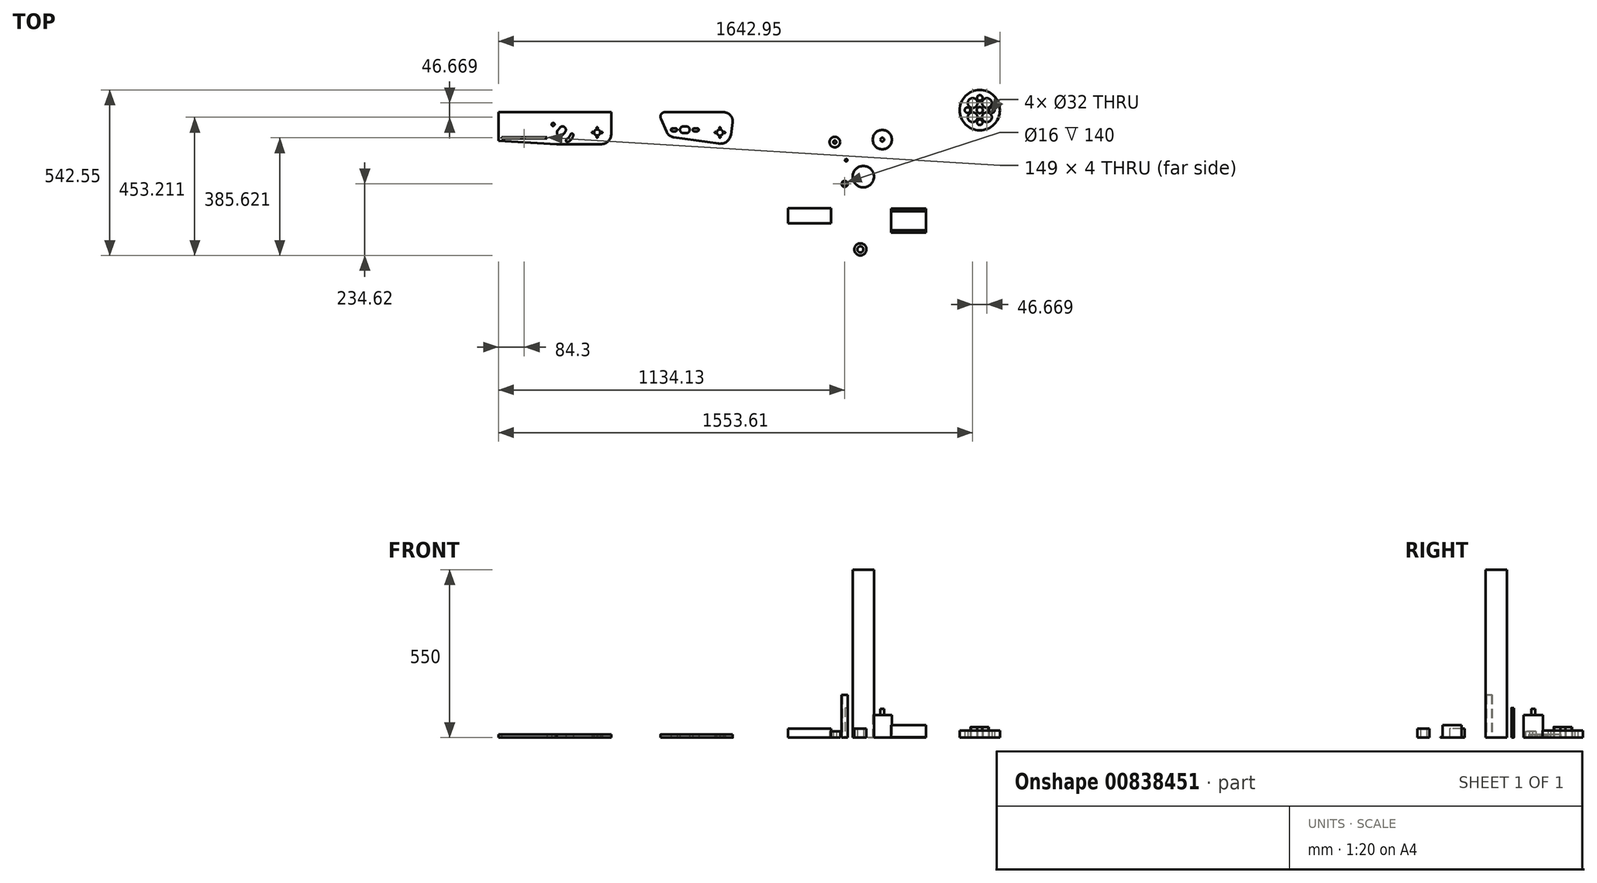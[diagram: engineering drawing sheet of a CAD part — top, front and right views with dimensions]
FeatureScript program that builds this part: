
annotation { "Feature Type Name" : "Feature", "Feature Type Description" : "" }
export const myFeature = defineFeature(function(context is Context, id is Id, definition is map)
    precondition{}
    {
        {
            var Q0;
            Q0=qCreatedBy(makeId("Top.planeOp"),FACE);
            var sketch = newSketch(context, id + "F0", { "sketchPlane" : qUnion([Q0])});
            skCircle(sketch, "E0", {"center": v(363.58, 0) * mm, "radius": 31.5 * mm});
            skCircle(sketch, "E1", {"center": v(683.06, 96.7) * mm, "radius": 66 * mm});
            skCircle(sketch, "E2", {"center": v(208.04, -8.08) * mm, "radius": 17.5 * mm});
            skCircle(sketch, "E3", {"center": v(683.06, 96.7) * mm, "radius": 30 * mm});
            skCircle(sketch, "E4", {"center": v(208.04, -8.08) * mm, "radius": 8 * mm});
            skCircle(sketch, "E5", {"center": v(240.24, -145.22) * mm, "radius": 10 * mm});
            skCircle(sketch, "E6", {"center": v(683.06, 96.7) * mm, "radius": 10 * mm});
            skCircle(sketch, "E7", {"center": v(208.04, -8.08) * mm, "radius": 5 * mm});
            skCircle(sketch, "E8", {"center": v(301.26, -121.43) * mm, "radius": 35 * mm});
            skLineSegment(sketch, "E9.top", {"start": v(-319.76, 7.6) * mm, "end": v(-172.04, -13.07) * mm});
            skLineSegment(sketch, "E9.left", {"start": v(-371.65, 89.78) * mm, "end": v(-343.03, 25.16) * mm});
            skLineSegment(sketch, "E9.right", {"start": v(-126.77, 55.36) * mm, "end": v(-132.57, 16.43) * mm});
            skCircle(sketch, "E10", {"center": v(-168.45, 23.28) * mm, "radius": 10 * mm});
            skCircle(sketch, "E11", {"center": v(-283.3, 32.28) * mm, "radius": 11 * mm, "construction": true});
            skCircle(sketch, "E12", {"center": v(-168.45, 23.28) * mm, "radius": 31.5 * mm, "construction": true});
            skLineSegment(sketch, "E13", {"start": v(-156.45, 89.78) * mm, "end": v(-371.65, 89.78) * mm});
            skLineSegment(sketch, "E14", {"start": v(-371.65, 89.78) * mm, "end": v(-371.65, 89.78) * mm});
            skCircle(sketch, "E15", {"center": v(245.41, -67.65) * mm, "radius": 4 * mm});
            skLineSegment(sketch, "E16.bottom", {"start": v(506.27, -226.68) * mm, "end": v(392.27, -226.68) * mm});
            skLineSegment(sketch, "E16.top", {"start": v(506.27, -304.68) * mm, "end": v(392.27, -304.68) * mm});
            skLineSegment(sketch, "E16.left", {"start": v(506.27, -226.68) * mm, "end": v(506.27, -304.68) * mm});
            skLineSegment(sketch, "E16.right", {"start": v(392.27, -226.68) * mm, "end": v(392.27, -304.68) * mm});
            skLineSegment(sketch, "E17", {"start": v(392.27, -234.68) * mm, "end": v(506.27, -234.68) * mm});
            skLineSegment(sketch, "E18", {"start": v(392.27, -296.68) * mm, "end": v(506.27, -296.68) * mm});
            skLineSegment(sketch, "E19", {"start": v(-318.8, 32.28) * mm, "end": v(-247.8, 32.28) * mm, "construction": true});
            skCircle(sketch, "E20", {"center": v(-247.8, 32.28) * mm, "radius": 5 * mm, "construction": true});
            skCircle(sketch, "E21", {"center": v(-318.8, 32.28) * mm, "radius": 5 * mm, "construction": true});
            skLineSegment(sketch, "E22", {"start": v(-358.36, 59.78) * mm, "end": v(-126.12, 59.78) * mm, "construction": true});
            skCircle(sketch, "E23", {"center": v(-283.3, 32.28) * mm, "radius": 27.5 * mm, "construction": true});
            skLineSegment(sketch, "E24.bottom", {"start": v(196.15, -225.01) * mm, "end": v(54.15, -225.01) * mm});
            skLineSegment(sketch, "E24.top", {"start": v(196.15, -274.01) * mm, "end": v(54.15, -274.01) * mm});
            skLineSegment(sketch, "E24.left", {"start": v(196.15, -225.01) * mm, "end": v(196.15, -274.01) * mm});
            skLineSegment(sketch, "E24.right", {"start": v(54.15, -225.01) * mm, "end": v(54.15, -274.01) * mm});
            skLineSegment(sketch, "E25", {"start": v(-214.95, -7.07) * mm, "end": v(-214.95, 89.78) * mm, "construction": true});
            skLineSegment(sketch, "E26", {"start": v(579.92, -80.42) * mm, "end": v(579.92, -80.42) * mm});
            skLineSegment(sketch, "E27.bottom", {"start": v(651.92, -162.42) * mm, "end": v(577.92, -162.42) * mm});
            skLineSegment(sketch, "E27.top", {"start": v(651.92, -80.42) * mm, "end": v(577.92, -80.42) * mm});
            skLineSegment(sketch, "E27.left", {"start": v(651.92, -162.42) * mm, "end": v(651.92, -80.42) * mm});
            skLineSegment(sketch, "E27.right", {"start": v(577.92, -162.42) * mm, "end": v(577.92, -80.42) * mm});
            skPoint(sketch, "E27.middle", {"position": v(614.92, -121.42) * mm});
            skLineSegment(sketch, "E28", {"start": v(-224.75, -5.7) * mm, "end": v(-224.75, 89.78) * mm, "construction": true});
            skCircle(sketch, "E29", {"center": v(-570.76, 23.28) * mm, "radius": 10 * mm});
            skCircle(sketch, "E30", {"center": v(-684.4, 32.28) * mm, "radius": 11 * mm});
            skCircle(sketch, "E31", {"center": v(-570.76, 23.28) * mm, "radius": 31.5 * mm, "construction": true});
            skLineSegment(sketch, "E32", {"start": v(-715.29, 49.78) * mm, "end": v(-653.52, 14.78) * mm, "construction": true});
            skCircle(sketch, "E33", {"center": v(-653.52, 14.78) * mm, "radius": 5 * mm});
            skCircle(sketch, "E34", {"center": v(-715.29, 49.78) * mm, "radius": 5 * mm});
            skCircle(sketch, "E35", {"center": v(-684.4, 32.28) * mm, "radius": 27.5 * mm, "construction": true});
            skLineSegment(sketch, "E36.bottom", {"start": v(-893.89, 89.78) * mm, "end": v(-524.46, 89.78) * mm});
            skLineSegment(sketch, "E36.top", {"start": v(-893.89, -15.22) * mm, "end": v(-559.46, -15.22) * mm});
            skLineSegment(sketch, "E36.left", {"start": v(-1035.89, 60.78) * mm, "end": v(-1035.89, 59.78) * mm});
            skLineSegment(sketch, "E36.right", {"start": v(-524.46, 89.78) * mm, "end": v(-524.46, 19.78) * mm});
            skLineSegment(sketch, "E37", {"start": v(-1035.89, 59.78) * mm, "end": v(-524.46, 59.78) * mm, "construction": true});
            skLineSegment(sketch, "E38", {"start": v(-725.29, 89.78) * mm, "end": v(-725.29, -15.22) * mm, "construction": true});
            skLineSegment(sketch, "E39", {"start": v(-735.09, 89.78) * mm, "end": v(-735.09, -15.22) * mm, "construction": true});
            skLineSegment(sketch, "E40", {"start": v(-534.26, 89.78) * mm, "end": v(-534.26, -15.22) * mm, "construction": true});
            skLineSegment(sketch, "E41", {"start": v(-884.09, 89.78) * mm, "end": v(-884.09, -15.22) * mm, "construction": true});
            skLineSegment(sketch, "E42", {"start": v(-893.89, 89.78) * mm, "end": v(-893.89, -15.22) * mm});
            skLineSegment(sketch, "E43", {"start": v(-884.09, 7.78) * mm, "end": v(-735.09, 7.78) * mm});
            skCircle(sketch, "E44", {"center": v(-684.4, 32.28) * mm, "radius": 66 * mm, "construction": true});
            skCircle(sketch, "E45", {"center": v(-570.76, 23.28) * mm, "radius": 19 * mm, "construction": true});
            skLineSegment(sketch, "E46", {"start": v(-563.63, -7.4) * mm, "end": v(-669.46, -32) * mm, "construction": true});
            skLineSegment(sketch, "E47", {"start": v(-558.89, 52.46) * mm, "end": v(-659.53, 93.41) * mm, "construction": true});
            skCircle(sketch, "E48", {"center": v(-668.05, -3.22) * mm, "radius": 5 * mm});
            skCircle(sketch, "E49", {"center": v(-555.76, 23.28) * mm, "radius": 2.25 * mm});
            skCircle(sketch, "E50", {"center": v(-585.76, 23.28) * mm, "radius": 2.25 * mm});
            skCircle(sketch, "E51", {"center": v(-570.76, 38.28) * mm, "radius": 2.25 * mm});
            skCircle(sketch, "E52", {"center": v(-570.76, 8.28) * mm, "radius": 2.25 * mm});
            skLineSegment(sketch, "E53", {"start": v(-884.09, 7.78) * mm, "end": v(-884.09, 3.78) * mm});
            skLineSegment(sketch, "E54", {"start": v(-884.09, 3.78) * mm, "end": v(-735.09, 3.78) * mm});
            skLineSegment(sketch, "E55", {"start": v(-735.09, 3.78) * mm, "end": v(-735.09, 7.78) * mm});
            skPoint(sketch, "E56.visualSharp", {"position": v(-524.46, -15.22) * mm});
            skArc(sketch, "E56.filletArc", {"start": v(-559.46, -15.22) * mm, "mid": v(-534.7, -4.97) * mm, "end": v(-524.46, 19.78) * mm});
            skArc(sketch, "E57", {"start": v(-670.7, 1.02) * mm, "mid": v(-663.16, 7.7) * mm, "end": v(-658.22, 16.48) * mm});
            skArc(sketch, "E58", {"start": v(-665.4, -7.46) * mm, "mid": v(-655.38, 1.42) * mm, "end": v(-648.81, 13.08) * mm});
            skLineSegment(sketch, "E59", {"start": v(-715.29, 49.78) * mm, "end": v(-668.05, -3.22) * mm, "construction": true});
            skCircle(sketch, "E60", {"center": v(-691.67, 23.28) * mm, "radius": 11 * mm});
            skArc(sketch, "E61", {"start": v(-698.99, 31.5) * mm, "mid": v(-696.23, 34.4) * mm, "end": v(-693.97, 37.7) * mm});
            skArc(sketch, "E62", {"start": v(-684.35, 15.07) * mm, "mid": v(-679.1, 20.57) * mm, "end": v(-674.83, 26.86) * mm});
            skCircle(sketch, "E63", {"center": v(-153.45, 23.28) * mm, "radius": 2.25 * mm});
            skCircle(sketch, "E64", {"center": v(-183.45, 23.28) * mm, "radius": 2.25 * mm});
            skCircle(sketch, "E65", {"center": v(-168.45, 38.28) * mm, "radius": 2.25 * mm});
            skCircle(sketch, "E66", {"center": v(-168.45, 8.28) * mm, "radius": 2.25 * mm});
            skCircle(sketch, "E67", {"center": v(-168.45, 23.28) * mm, "radius": 19 * mm, "construction": true});
            skCircle(sketch, "E68", {"center": v(-313.8, 32.28) * mm, "radius": 5 * mm});
            skCircle(sketch, "E69", {"center": v(-323.8, 32.28) * mm, "radius": 5 * mm});
            skLineSegment(sketch, "E70", {"start": v(-323.8, 37.28) * mm, "end": v(-313.8, 37.28) * mm});
            skLineSegment(sketch, "E71", {"start": v(-313.8, 27.28) * mm, "end": v(-323.8, 27.28) * mm});
            skCircle(sketch, "E72", {"center": v(-283.3, 32.28) * mm, "radius": 66 * mm, "construction": true});
            skLineSegment(sketch, "E73", {"start": v(-162.08, 5.38) * mm, "end": v(-261.16, -29.9) * mm, "construction": true});
            skLineSegment(sketch, "E74", {"start": v(-159.37, 39.97) * mm, "end": v(-251.75, 90.25) * mm, "construction": true});
            skPoint(sketch, "E75.visualSharp", {"position": v(-137.68, -17.88) * mm});
            skArc(sketch, "E75.filletArc", {"start": v(-172.04, -13.07) * mm, "mid": v(-146.23, -6.44) * mm, "end": v(-132.57, 16.43) * mm});
            skCircle(sketch, "E76", {"center": v(-242.8, 32.28) * mm, "radius": 5 * mm});
            skCircle(sketch, "E77", {"center": v(-252.8, 32.28) * mm, "radius": 5 * mm});
            skLineSegment(sketch, "E78", {"start": v(-252.8, 37.28) * mm, "end": v(-242.8, 37.28) * mm});
            skLineSegment(sketch, "E79", {"start": v(-242.8, 27.28) * mm, "end": v(-252.8, 27.28) * mm});
            skCircle(sketch, "E80", {"center": v(-278.3, 32.28) * mm, "radius": 11 * mm});
            skCircle(sketch, "E81", {"center": v(-288.3, 32.28) * mm, "radius": 11 * mm});
            skLineSegment(sketch, "E82", {"start": v(-288.3, 43.28) * mm, "end": v(-278.3, 43.28) * mm});
            skLineSegment(sketch, "E83", {"start": v(-278.3, 21.28) * mm, "end": v(-288.3, 21.28) * mm});
            skPoint(sketch, "E84.visualSharp", {"position": v(-336.28, 9.9) * mm});
            skArc(sketch, "E84.filletArc", {"start": v(-343.03, 25.16) * mm, "mid": v(-333.67, 13.36) * mm, "end": v(-319.76, 7.6) * mm});
            skArc(sketch, "E85", {"start": v(-348.6, 89.78) * mm, "mid": v(-361.17, 82.96) * mm, "end": v(-362.32, 68.7) * mm});
            skPoint(sketch, "E86.visualSharp", {"position": v(-121.65, 89.78) * mm});
            skArc(sketch, "E86.filletArc", {"start": v(-126.77, 55.36) * mm, "mid": v(-133.73, 79.37) * mm, "end": v(-156.45, 89.78) * mm});
            skLineSegment(sketch, "E87", {"start": v(-371.65, 89.78) * mm, "end": v(-283.3, 32.28) * mm, "construction": true});
            skLineSegment(sketch, "E88", {"start": v(-343.6, 74.78) * mm, "end": v(-343.6, 26.53) * mm, "construction": true});
            skLineSegment(sketch, "E89", {"start": v(-328.8, 32.28) * mm, "end": v(-328.8, 89.78) * mm, "construction": true});
            skCircle(sketch, "E90", {"center": v(614.92, -125.67) * mm, "radius": 5.25 * mm});
            skPoint(sketch, "E91", {"position": v(614.92, -120.42) * mm});
            skPoint(sketch, "E92", {"position": v(614.92, -110.42) * mm});
            skLineSegment(sketch, "E93", {"start": v(-382.03, 54.78) * mm, "end": v(-102.81, 54.78) * mm, "construction": true});
            skLineSegment(sketch, "E94", {"start": v(-382.03, 44.78) * mm, "end": v(-102.81, 44.78) * mm, "construction": true});
            skPoint(sketch, "E95", {"position": v(482.25, 720.36) * mm});
            skPoint(sketch, "E96", {"position": v(567.95, 901.07) * mm});
            skLineSegment(sketch, "E97", {"start": v(383.5, 60.78) * mm, "end": v(-1168.06, 60.78) * mm, "construction": true});
            skPoint(sketch, "E98.orphan", {"position": v(-1035.89, 89.78) * mm});
            skLineSegment(sketch, "E99", {"start": v(-704.1, -15.22) * mm, "end": v(-893.89, -3.17) * mm});
            skCircle(sketch, "E100", {"center": v(291.76, -359.84) * mm, "radius": 20 * mm});
            skCircle(sketch, "E101", {"center": v(240.24, -145.22) * mm, "radius": 8 * mm});
            skCircle(sketch, "E102", {"center": v(291.76, -359.84) * mm, "radius": 10 * mm});
            skCircle(sketch, "E103", {"center": v(683.06, 136.7) * mm, "radius": 9 * mm});
            skCircle(sketch, "E104", {"center": v(659.72, 120.04) * mm, "radius": 16 * mm});
            skCircle(sketch, "E105", {"center": v(659.72, 73.37) * mm, "radius": 16 * mm});
            skCircle(sketch, "E106", {"center": v(683.06, 56.7) * mm, "radius": 9 * mm});
            skCircle(sketch, "E107", {"center": v(706.4, 73.37) * mm, "radius": 16 * mm});
            skCircle(sketch, "E108", {"center": v(706.4, 120.04) * mm, "radius": 16 * mm});
            skCircle(sketch, "E109", {"center": v(643.06, 96.7) * mm, "radius": 9 * mm});
            skCircle(sketch, "E110", {"center": v(723.06, 96.7) * mm, "radius": 9 * mm});
            skLineSegment(sketch, "E111", {"start": v(683.06, 136.7) * mm, "end": v(683.06, 56.7) * mm, "construction": true});
            skLineSegment(sketch, "E112", {"start": v(643.06, 96.7) * mm, "end": v(723.06, 96.7) * mm, "construction": true});
            skLineSegment(sketch, "E113", {"start": v(706.4, 120.04) * mm, "end": v(659.72, 73.37) * mm, "construction": true});
            skLineSegment(sketch, "E114", {"start": v(659.72, 120.04) * mm, "end": v(706.4, 73.37) * mm, "construction": true});
            skCircle(sketch, "E115", {"center": v(683.06, 96.7) * mm, "radius": 49 * mm, "construction": true});
            skCircle(sketch, "E116", {"center": v(683.06, 96.7) * mm, "radius": 31 * mm, "construction": true});
            skCircle(sketch, "E117", {"center": v(683.06, 96.7) * mm, "radius": 17 * mm, "construction": true});
            skSolve(sketch);
        }
        {
            var Q0;
            Q0=makeQuery(id+"F0.imprint","IMPRINT",FACE,{"disambiguationData":[TD([[makeQuery(id+"F0.imprint","IMPRINT",EDGE,{"derivedFrom":sQuery(id+"F0.wireOp",EDGE,"E0")}),1.0]])]});
            extrude(context, id + "F1", {"entities" : qUnion([Q0]), "depth" : 74 * mm, "offsetDistance" : 25 * mm});
        }
        {
            var Q0;
            Q0=makeQuery(id+"F1.opExtrude","CAP_FACE",FACE,{"disambiguationData":[OSD([sQuery(id+"F0.wireOp",EDGE,"E0")])],"isStart":false});
            var sketch = newSketch(context, id + "F2", { "sketchPlane" : qUnion([Q0])});
            skCircle(sketch, "E118", {"center": v(363.58, 0) * mm, "radius": 6 * mm});
            skSolve(sketch);
        }
        {
            var Q0;
            Q0 = qSketchRegion(id + "F2", true);
            extrude(context, id + "F3", {"entities" : qUnion([Q0]), "operationType" : NewBodyOperationType.ADD, "depth" : 20 * mm, "offsetDistance" : 25 * mm});
        }
        {
            var Q0;
            Q0=makeQuery(id+"F0.imprint","IMPRINT",FACE,{"disambiguationData":[TD([[makeQuery(id+"F0.imprint","IMPRINT",EDGE,{"derivedFrom":sQuery(id+"F0.wireOp",EDGE,"E6")}),-1.0]])]});
            var Q1;
            Q1=makeQuery(id+"F0.imprint","IMPRINT",FACE,{"disambiguationData":[TD([[makeQuery(id+"F0.imprint","IMPRINT",EDGE,{"derivedFrom":sQuery(id+"F0.wireOp",EDGE,"E1")}),1.0]])]});
            extrude(context, id + "F4", {"entities" : qUnion([Q0, Q1]), "depth" : 22.5 * mm, "offsetDistance" : 25 * mm});
        }
        {
            var Q0;
            Q0=makeQuery(id+"F0.imprint","IMPRINT",FACE,{"disambiguationData":[TD([[makeQuery(id+"F0.imprint","IMPRINT",EDGE,{"derivedFrom":sQuery(id+"F0.wireOp",EDGE,"E3")}),1.0]])]});
            extrude(context, id + "F5", {"entities" : qUnion([Q0]), "depth" : 35 * mm, "offsetDistance" : 25 * mm});
        }
        {
            var Q0;
            Q0=makeQuery(id+"F0.imprint","IMPRINT",FACE,{"disambiguationData":[TD([[makeQuery(id+"F0.imprint","IMPRINT",EDGE,{"derivedFrom":sQuery(id+"F0.wireOp",EDGE,"E2")}),1.0]])]});
            var Q1;
            Q1=makeQuery(id+"F0.imprint","IMPRINT",FACE,{"disambiguationData":[TD([[makeQuery(id+"F0.imprint","IMPRINT",EDGE,{"derivedFrom":sQuery(id+"F0.wireOp",EDGE,"E4")}),1.0]])]});
            extrude(context, id + "F6", {"entities" : qUnion([Q0, Q1]), "operationType" : NewBodyOperationType.ADD, "depth" : 20 * mm, "offsetDistance" : 25 * mm});
        }
        {
            var Q0;
            Q0=makeQuery(id+"F0.imprint","IMPRINT",FACE,{"disambiguationData":[TD([[makeQuery(id+"F0.imprint","IMPRINT",EDGE,{"derivedFrom":sQuery(id+"F0.wireOp",EDGE,"E5")}),1.0]])]});
            extrude(context, id + "F7", {"entities" : qUnion([Q0]), "depth" : 140 * mm, "offsetDistance" : 25 * mm});
        }
        {
            var Q0;
            Q0=makeQuery(id+"F0.imprint","IMPRINT",FACE,{"disambiguationData":[TD([[makeQuery(id+"F0.imprint","IMPRINT",EDGE,{"derivedFrom":sQuery(id+"F0.wireOp",EDGE,"E8")}),1.0]])]});
            extrude(context, id + "F8", {"entities" : qUnion([Q0]), "depth" : 550 * mm, "offsetDistance" : 25 * mm});
        }
        {
            var Q0;
            {var subQ5=sQuery(id+"F0.wireOp",EDGE,"E9.top");Q0=makeQuery(id+"F0.imprint","IMPRINT",FACE,{"disambiguationData":[TD([[makeQuery(id+"F0.imprint","IMPRINT",EDGE,{"derivedFrom":subQ5}),1.0]])]});}
            var Q1;
            {var subQ0=sQuery(id+"F0.wireOp",EDGE,"E14");Q1=makeQuery(id+"F0.imprint","IMPRINT",FACE,{"disambiguationData":[TD([[makeQuery(id+"F0.imprint","IMPRINT",EDGE,{"derivedFrom":subQ0}),1.0]])]});}
            var Q2;
            Q2=makeQuery(id+"F0.imprint","IMPRINT",FACE,{"disambiguationData":[TD([[makeQuery(id+"F0.imprint","IMPRINT",EDGE,{"derivedFrom":sQuery(id+"F0.wireOp",EDGE,"E29")}),-1.0]])]});
            var Q3;
            {var subQ1=sQuery(id+"F0.wireOp",EDGE,"E26");Q3=makeQuery(id+"F0.imprint","IMPRINT",FACE,{"disambiguationData":[TD([[makeQuery(id+"F0.imprint","IMPRINT",EDGE,{"derivedFrom":subQ1}),-1.0]])]});}
            extrude(context, id + "F9", {"entities" : qUnion([Q0, Q1, Q2, Q3]), "depth" : 9.8 * mm, "offsetDistance" : 25 * mm});
        }
        {
            var Q0;
            Q0=makeQuery(id+"F0.imprint","IMPRINT",FACE,{"disambiguationData":[TD([[makeQuery(id+"F0.imprint","IMPRINT",EDGE,{"derivedFrom":sQuery(id+"F0.wireOp",EDGE,"E15")}),1.0]])]});
            extrude(context, id + "F10", {"entities" : qUnion([Q0]), "depth" : 97 * mm, "offsetDistance" : 25 * mm});
        }
        {
            var Q0;
            {var subQ0=sQuery(id+"F0.wireOp",EDGE,"E17");Q0=makeQuery(id+"F0.imprint","IMPRINT",FACE,{"disambiguationData":[TD([[makeQuery(id+"F0.imprint","IMPRINT",EDGE,{"derivedFrom":subQ0}),-1.0]])]});}
            extrude(context, id + "F11", {"entities" : qUnion([Q0]), "depth" : 41 * mm, "offsetDistance" : 25 * mm});
        }
        {
            var Q0;
            {var subQ0=sQuery(id+"F0.wireOp",EDGE,"E16.bottom");Q0=makeQuery(id+"F0.imprint","IMPRINT",FACE,{"disambiguationData":[TD([[makeQuery(id+"F0.imprint","IMPRINT",EDGE,{"derivedFrom":subQ0}),1.0]])]});}
            var Q1;
            {var subQ0=sQuery(id+"F0.wireOp",EDGE,"E16.top");Q1=makeQuery(id+"F0.imprint","IMPRINT",FACE,{"disambiguationData":[TD([[makeQuery(id+"F0.imprint","IMPRINT",EDGE,{"derivedFrom":subQ0}),-1.0]])]});}
            extrude(context, id + "F12", {"entities" : qUnion([Q0, Q1]), "operationType" : NewBodyOperationType.ADD, "depth" : 2 * mm, "offsetDistance" : 25 * mm});
        }
        {
            var Q0;
            Q0=makeQuery(id+"F0.imprint","IMPRINT",FACE,{"disambiguationData":[TD([[makeQuery(id+"F0.imprint","IMPRINT",EDGE,{"derivedFrom":sQuery(id+"F0.wireOp",EDGE,"E24.bottom")}),1.0]])]});
            extrude(context, id + "F13", {"entities" : qUnion([Q0]), "depth" : 29 * mm, "offsetDistance" : 25 * mm});
        }
        {
            var Q0;
            Q0=makeQuery(id+"F0.imprint","IMPRINT",FACE,{"disambiguationData":[TD([[makeQuery(id+"F0.imprint","IMPRINT",EDGE,{"derivedFrom":sQuery(id+"F0.wireOp",EDGE,"E100")}),1.0]])]});
            extrude(context, id + "F14", {"entities" : qUnion([Q0]), "depth" : 29.7 * mm, "offsetDistance" : 25 * mm});
        }
    });
